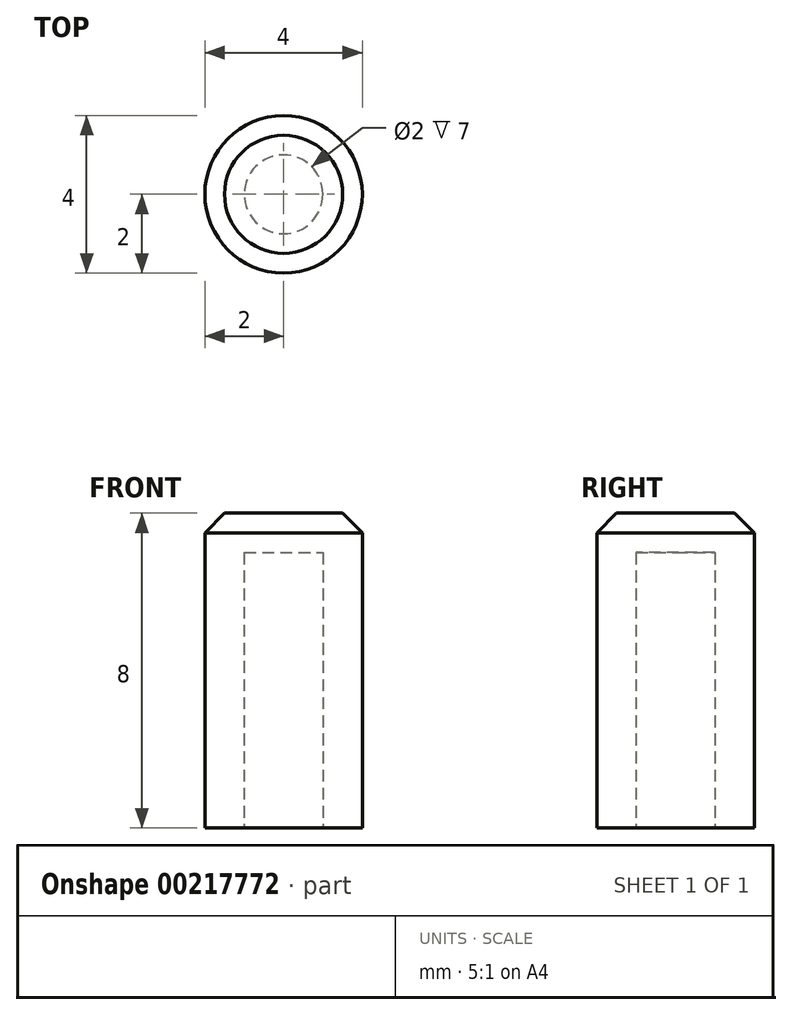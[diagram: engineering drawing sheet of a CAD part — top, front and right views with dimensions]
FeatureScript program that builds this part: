
annotation { "Feature Type Name" : "Feature", "Feature Type Description" : "" }
export const myFeature = defineFeature(function(context is Context, id is Id, definition is map)
    precondition{}
    {
        {
            var Q0;
            Q0=qCreatedBy(makeId("Top.planeOp"),FACE);
            var sketch = newSketch(context, id + "F0", { "sketchPlane" : qUnion([Q0])});
            skCircle(sketch, "E0", {"center": v(0, 0) * mm, "radius": 2 * mm});
            skSolve(sketch);
        }
        {
            var Q0;
            Q0 = qSketchRegion(id + "F0", true);
            extrude(context, id + "F1", {"entities" : qUnion([Q0]), "depth" : 8 * mm});
        }
        {
            var Q0;
            Q0=makeQuery(id+"F1.opExtrude","CAP_FACE",FACE,{"disambiguationData":[OSD([sQuery(id+"F0.wireOp",EDGE,"E0")])],"isStart":true});
            var sketch = newSketch(context, id + "F2", { "sketchPlane" : qUnion([Q0])});
            skCircle(sketch, "E1", {"center": v(0, 0) * mm, "radius": 1 * mm});
            skSolve(sketch);
        }
        {
            var Q0;
            Q0 = qSketchRegion(id + "F2", true);
            extrude(context, id + "F3", {"entities" : qUnion([Q0]), "operationType" : NewBodyOperationType.REMOVE, "oppositeDirection" : true, "depth" : 7 * mm});
        }
        {
            var Q0;
            Q0=makeQuery(id+"F1.opExtrude","CAP_EDGE",EDGE,{"disambiguationData":[OSD([sQuery(id+"F0.wireOp",EDGE,"E0")])],"isStart":false});
            chamfer(context, id + "F4", {"entities" : qUnion([Q0]), "width" : .5 * mm, "tangentPropagation" : true});
        }
    });
